# Revit family: Equipos de bombeo hasta 2 bombas principales
name_source: partatom
category: Modelos genéricos
units: mm (PartAtom-declared; Revit-internal decimal feet)

## family parameters
Compartido = No
Corte con vacíos al cargar = Sí
Cota de conector redondo = Diámetro de uso
Número OmniClass = 23.65.55.00
Puede alojar armadura = No
Punto de cálculo de habitación = No
Se basa en plano de trabajo = No
Siempre vertical = Sí
Tipo de pieza = Normal
Título OmniClass = Distribution of Supplied Liquids/Gases

## types (2) — shared parameters
Acero = Acero.00
Descripción = Equipo de bombeo compuesto por electro bombas de tipo volumétrico de pistones cerámicos de caudal 40L/min, presión 140 bar, motor eléctrico trifásico de 220/380V y 15 C.V (11.04 kw) más una bomba jockey con caudal 2.6 l/min regulada a unapresión entre 30 y 40 bar, con motor eléctrico trifásico de 380 V y 3 C.V (2,2 kw). El cuadro de control eléctrico que regula el funcionamiento de los equipos está diseñado según la norma UNE 23500 y permite la emisión de alarmas a distancia. El equipo está compuesto por una bomba controlada por un variador de frecuencia y la otra a través de un arrancador suave. Se entrega montado sobre bancada universal, regulado de acuerdo a la presión de trabajo según proyecto y compobado su funcionamiento.
El equipo de bombeo se entrega con:

Latiguillo flexible de alta presión para la impulsión,de 1” y de 600 mm de longitud. Conexión macho giratoria rosca BSP 1″.
Latiguillo flexible de alta presión para retorno, de 1” y de 600 mm de longitud. Conexión macho giratoria rosca BSP 1″.
Latiguillo de aspiración de baja presión para la aspiración, de 2” y 600 mm de longitud. Conexión macho rosca BSP 2″.
* Sin incluir desplazamientos.
* Salvo indicación por parte del cliente, esta prueba de funcionamiento no se realiza sobre el riesgo a proteger, sino utilizando el circuito de prueba y retorno del equipo de bombeo.
Fabricante = Aguilera Extinción
Símbolo = Sí
Símbolo texto modelo = Sí
URL = http://aguilera.es
X = 900 mm  [stored 2.95276 ft]
Y0 = 98 mm  [stored 0.321522 ft]
Z = 1750 mm  [stored 5.74147 ft]
mat.01 = mat.01
mat.02a = mat.02a
mat.02b = mat.02b
mat.03 = mat.03
mat.04 = mat.04
mat.05 = mat.05
t = 5 mm  [stored 0.0164042 ft]
x1 = 570 mm  [stored 1.87008 ft]
x2 = 620 mm
y2 = 33 mm
z1 = 40 mm  [stored 0.131234 ft]
z2 = 460 mm  [stored 1.50919 ft]
z3 = 270 mm  [stored 0.885827 ft]
z4 = 1000 mm  [stored 3.28084 ft]
Ø = 40 mm  [stored 0.131234 ft]

## per-type parameters (varying)
| type | Electric Pumps | Modelo | N | V | Y | flujo | potencia | y1 | y_Electric | Ø1 | Ø2 |
| Equipo de bombeo de 1 bomba principal (tub. Húmeda) | 1 | AN/GAH1-40 | 2 | No | 1100 mm  [stored 3.60892 ft] | 40.0 L/s | 15000 W | 805 mm | 1 mm  [stored 0.00328084 ft] | 0 mm  [stored 0 ft] | 0 mm  [stored 0 ft] |
| Equipo de bombeo de 2 bombas principales (tub. Húmeda) | 2 | AN/GAH2-40 | 3 | Sí | 1500 mm  [stored 4.92126 ft] | 80.0 L/s | 26000 W | 1185 mm  [stored 3.8878 ft] | 380 mm | 25 mm  [stored 0.082021 ft] | 51 mm |

note: [stored X ft] marks values corroborated as IEEE doubles in the binary element streams (Revit-internal decimal feet)
